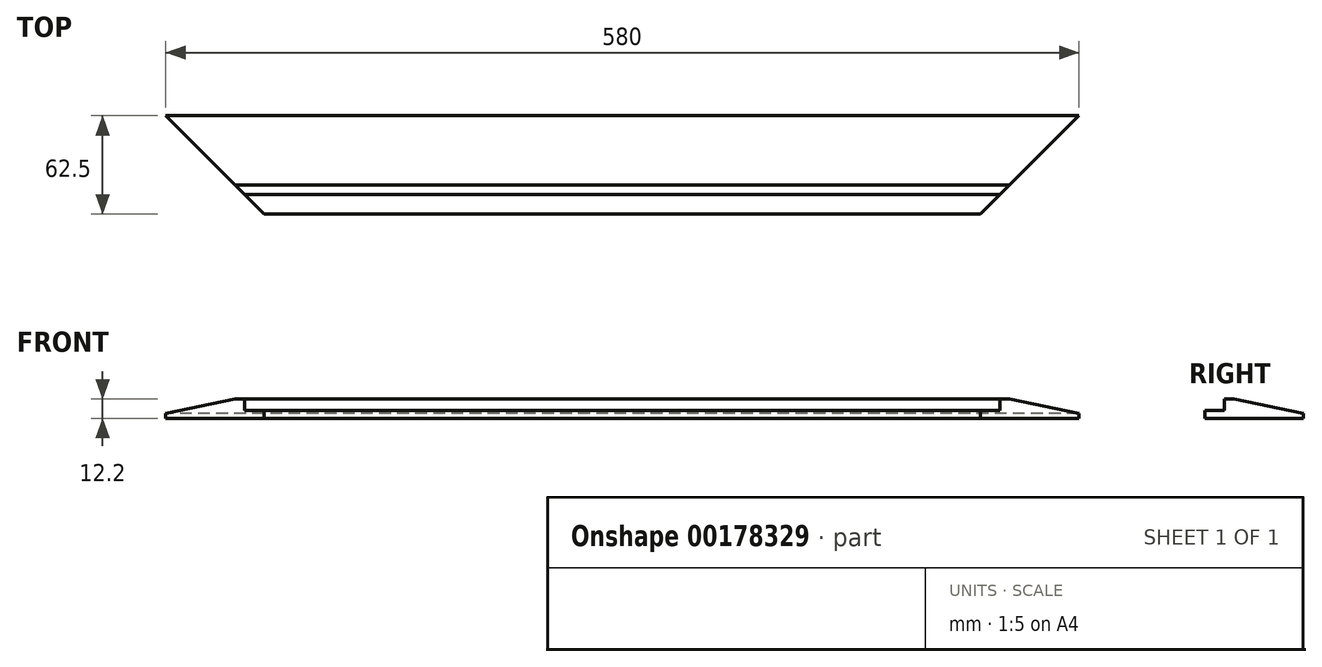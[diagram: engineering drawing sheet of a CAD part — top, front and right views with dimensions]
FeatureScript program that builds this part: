
annotation { "Feature Type Name" : "Feature", "Feature Type Description" : "" }
export const myFeature = defineFeature(function(context is Context, id is Id, definition is map)
    precondition{}
    {
        {
            var Q0;
            Q0=qCreatedBy(makeId("Right.planeOp"),FACE);
            var sketch = newSketch(context, id + "F0", { "sketchPlane" : qUnion([Q0])});
            skLineSegment(sketch, "E0", {"start": v(0, 0) * mm, "end": v(62.5, 0) * mm});
            skLineSegment(sketch, "E1", {"start": v(62.5, 0) * mm, "end": v(62.5, 3) * mm});
            skLineSegment(sketch, "E2", {"start": v(18.5, 12.2) * mm, "end": v(12.5, 12.2) * mm});
            skLineSegment(sketch, "E3", {"start": v(0, 5) * mm, "end": v(0, 0) * mm});
            skLineSegment(sketch, "E4.0", {"start": v(24.24, 11) * mm, "end": v(12.5, 11) * mm});
            skLineSegment(sketch, "E5.0", {"start": v(52.93, 5) * mm, "end": v(0, 5) * mm});
            skLineSegment(sketch, "E6.0", {"start": v(12.5, 12.2) * mm, "end": v(12.5, 0) * mm});
            skPoint(sketch, "E7.orphan", {"position": v(0, 12.2) * mm});
            skLineSegment(sketch, "E8.0", {"start": v(0, 3) * mm, "end": v(62.5, 3) * mm});
            skLineSegment(sketch, "E9.0", {"start": v(18.5, 12.2) * mm, "end": v(18.5, 0) * mm});
            skLineSegment(sketch, "E10", {"start": v(62.5, 3) * mm, "end": v(18.5, 12.2) * mm});
            skSolve(sketch);
        }
        {
            var Q0;
            Q0 = qSketchRegion(id + "F0", true);
            extrude(context, id + "F1", {"entities" : qUnion([Q0]), "depth" : 580 * mm});
        }
        {
            var Q0;
            Q0=qCreatedBy(makeId("Top.planeOp"),FACE);
            var sketch = newSketch(context, id + "F2", { "sketchPlane" : qUnion([Q0])});
            skLineSegment(sketch, "E11", {"start": v(0, 0) * mm, "end": v(0, 62.5) * mm});
            skLineSegment(sketch, "E12", {"start": v(62.5, 0) * mm, "end": v(0, 62.5) * mm});
            skLineSegment(sketch, "E13", {"start": v(62.5, 0) * mm, "end": v(0, 0) * mm});
            skLineSegment(sketch, "E14", {"start": v(0, 0) * mm, "end": v(62.5, 0) * mm});
            skSolve(sketch);
        }
        {
            var Q0;
            Q0 = qSketchRegion(id + "F2", true);
            extrude(context, id + "F3", {"entities" : qUnion([Q0]), "operationType" : NewBodyOperationType.REMOVE, "oppositeDirection" : true, "depth" : 100 * mm, "symmetric" : true});
        }
        {
            var Q0;
            Q0=qCreatedBy(makeId("Top.planeOp"),FACE);
            var sketch = newSketch(context, id + "F4", { "sketchPlane" : qUnion([Q0])});
            skLineSegment(sketch, "E15", {"start": v(0, 0) * mm, "end": v(517.5, 0) * mm});
            skLineSegment(sketch, "E16", {"start": v(517.5, 0) * mm, "end": v(580, 62.5) * mm});
            skLineSegment(sketch, "E17", {"start": v(580, 62.5) * mm, "end": v(580, 0) * mm});
            skLineSegment(sketch, "E18", {"start": v(580, 0) * mm, "end": v(517.5, 0) * mm});
            skSolve(sketch);
        }
        {
            var Q0;
            Q0 = qSketchRegion(id + "F4", true);
            var Q1;
            Q1=sQuery(id+"F4.wireOp",EDGE,"E18");
            var Q2;
            Q2=sQuery(id+"F4.wireOp",EDGE,"E16");
            var Q3;
            Q3=sQuery(id+"F4.wireOp",EDGE,"E17");
            extrude(context, id + "F5", {"entities" : qUnion([Q0]), "operationType" : NewBodyOperationType.REMOVE, "surfaceEntities" : qUnion([Q1, Q2, Q3]), "oppositeDirection" : true, "depth" : 100 * mm, "symmetric" : true});
        }
    });
